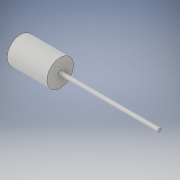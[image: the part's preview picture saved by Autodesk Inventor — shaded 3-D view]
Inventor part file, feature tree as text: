
AUTODESK INVENTOR PART (.ipt)
format: ipt  version: 2018 (Build 220112000, 112)  size: 98,304 bytes
history: native  units: in
note: dims shown in document units (in); Inventor stores cm internally (conversion verified against a paired STEP export)
features: revolve x1, sketch x1
ambient origin geometry x8: Origin, YZ Plane, XZ Plane, XY Plane, X Axis, Y Axis, Z Axis, Center Point
bodies: Solid1 (feature_tree)
feature tree (2):
  revolve  "Revolution1"  [1 undecoded]
  sketch  "Sketch1"  dims[d0=0.125in d1=7.5in d2=1.0in d3=3.0in d4=90.0deg]
note: 1 required parameter value undecoded (feature->parameter linkage not recoverable at this tier; creation-order binding heuristic only, values carry confidence <= 0.55)
